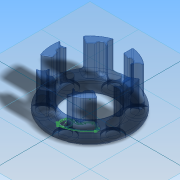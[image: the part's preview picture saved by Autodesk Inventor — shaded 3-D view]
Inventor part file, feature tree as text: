
AUTODESK INVENTOR PART (.ipt)
format: ipt  version: 2015 (Build 190159000, 159)  size: 869,376 bytes
history: native  units: in
note: dims shown in document units (in); Inventor stores cm internally (conversion verified against a paired STEP export)
features: fillet x5, other x3, extrude x3, sketch x2, chamfer x1, hole x1, pattern_circular x1
ambient origin geometry x8: Origin, YZ Plane, XZ Plane, XY Plane, X Axis, Y Axis, Z Axis, Center Point
bodies: Solid1 (feature_tree)
feature tree (16):
  other  "Wheel Insert Sketch.ipt"
  extrude  "Base"  Depth=0.3937in TaperAngle=0.0deg
  chamfer  "Chamfer2"  Distance=2.3622in Angle=360.0deg
  extrude  "Spoke"  Depth=0.1in
  hole  "Hole1"  [1 undecoded]
  fillet  "Fillet2"  Radius=0.01in
  fillet  "Fillet4"  Radius=0.06in
  fillet  "Fillet5"  Radius=0.01in
  pattern_circular  "Circular Pattern1"  [2 undecoded]
  extrude  "Center Hole"  Depth=0.1in TaperAngle=45.0deg
  fillet  "Fillet3"  Radius=0.1in
  fillet  "Fillet7"  Radius=0.02in
  other  "Spokes"
  other  "Circles"
  sketch  "Sketch3"  dims[d0=0.3937in d1=0.585in d2=0.0in d3=2.3622in d4=360.0deg]
  sketch  "Sketch4"  dims[d6=0.25in d7=0.0in d11=0.214in d12=0.75in d13=0.38in d14=0.05in d15=0.5635in d16=1.0in d17=0.8108in d28=1.0in d29=1.0in d30=0.0in d33=0.01in d34=0.06in d35=0.01in d38=0.025in d39=0.25in d40=0.14in d41=45.0deg d42=0.1in d43=0.02in]
note: 3 required parameter values undecoded (feature->parameter linkage not recoverable at this tier; creation-order binding heuristic only, values carry confidence <= 0.55)
